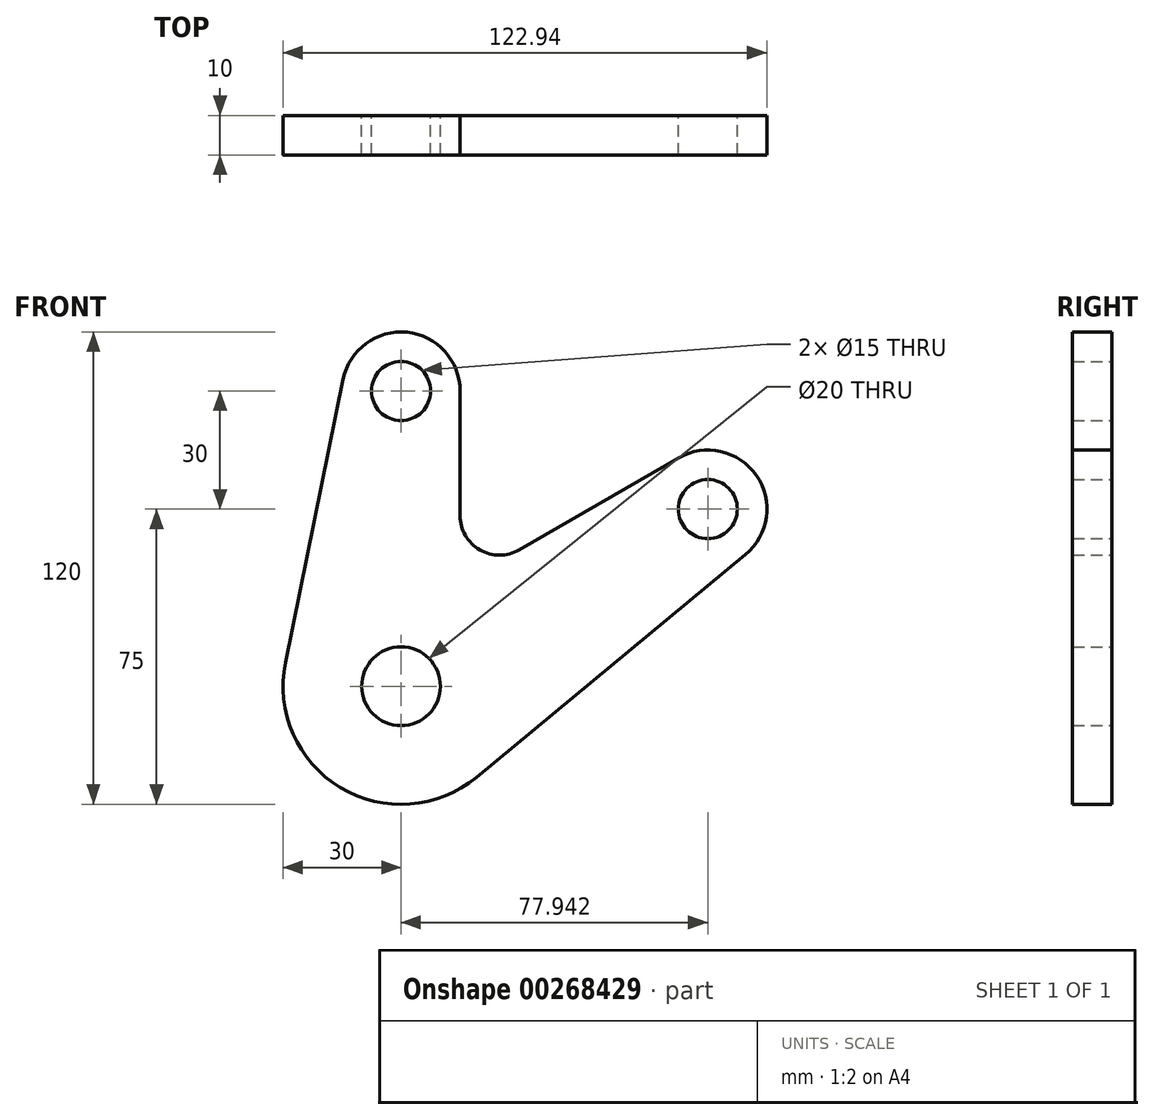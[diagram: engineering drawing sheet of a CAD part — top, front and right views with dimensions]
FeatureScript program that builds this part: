
annotation { "Feature Type Name" : "Feature", "Feature Type Description" : "" }
export const myFeature = defineFeature(function(context is Context, id is Id, definition is map)
    precondition{}
    {
        {
            var Q0;
            Q0=qCreatedBy(makeId("Front.planeOp"),FACE);
            var sketch = newSketch(context, id + "F0", { "sketchPlane" : qUnion([Q0])});
            skCircle(sketch, "E0", {"center": v(0, 0) * mm, "radius": 10 * mm});
            skCircle(sketch, "E1", {"center": v(0, 75) * mm, "radius": 7.5 * mm});
            skCircle(sketch, "E2", {"center": v(77.94, 45) * mm, "radius": 7.5 * mm});
            skLineSegment(sketch, "E3", {"start": v(19.12, -23.12) * mm, "end": v(87.5, 33.44) * mm});
            skLineSegment(sketch, "E4", {"start": v(30, 34.64) * mm, "end": v(70.44, 58) * mm});
            skLineSegment(sketch, "E5", {"start": v(15, 43.3) * mm, "end": v(15, 75) * mm});
            skLineSegment(sketch, "E6", {"start": v(-14.7, 78) * mm, "end": v(-29.4, 6) * mm});
            skArc(sketch, "E7", {"start": v(15, 75) * mm, "mid": v(1.5, 89.92) * mm, "end": v(-14.7, 78) * mm});
            skArc(sketch, "E8", {"start": v(87.5, 33.44) * mm, "mid": v(90.26, 53.56) * mm, "end": v(70.44, 58) * mm});
            skArc(sketch, "E9", {"start": v(-29.4, 6) * mm, "mid": v(-15.44, -25.72) * mm, "end": v(19.12, -23.12) * mm});
            skArc(sketch, "E10", {"start": v(15, 43.3) * mm, "mid": v(20, 34.64) * mm, "end": v(30, 34.64) * mm});
            skLineSegment(sketch, "E11", {"start": v(0, 0) * mm, "end": v(77.94, 45) * mm, "construction": true});
            skLineSegment(sketch, "E12", {"start": v(0, 75) * mm, "end": v(0, 0) * mm, "construction": true});
            skSolve(sketch);
        }
        {
            var Q0;
            Q0=makeQuery(id+"F0.imprint","IMPRINT",FACE,{"disambiguationData":[TD([[makeQuery(id+"F0.imprint","IMPRINT",EDGE,{"derivedFrom":sQuery(id+"F0.wireOp",EDGE,"E0")}),-1.0]])]});
            extrude(context, id + "F1", {"entities" : qUnion([Q0]), "depth" : 10 * mm});
        }
    });
